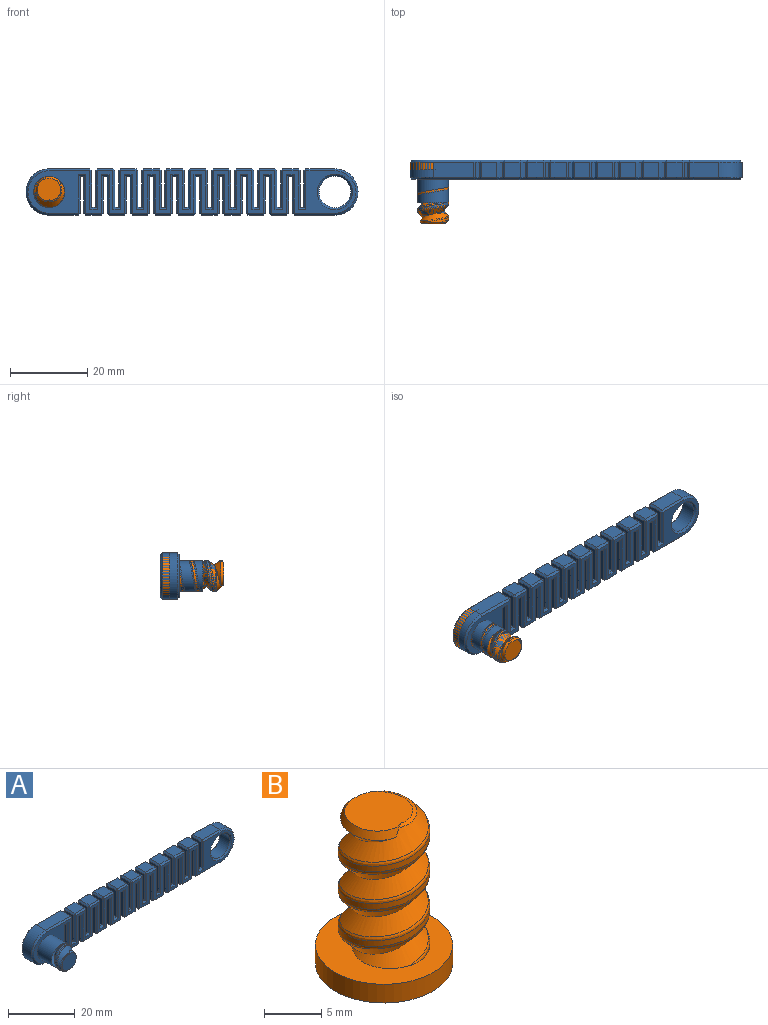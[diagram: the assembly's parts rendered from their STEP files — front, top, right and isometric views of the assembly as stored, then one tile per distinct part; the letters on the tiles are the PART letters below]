
ASSEMBLY  parts=2 mates=1
PART A: 390 faces, bbox 86.7x17.4x12.7 mm
  f0: cylinder r=4mm len=8mm, axis (0,1,0), area 152mm2, adj f1,f5,f91,f383
  f1: cylinder r=4mm len=8mm, axis (0,1,0), area 10.5mm2, adj f0,f4,f5,f386
  f2: bspline ~9.24x8mm, area 25.8mm2, adj f3,f4,f383,f387
  f3: bspline ~9.24x8mm, area 32.1mm2, adj f2,f5,f383,f387,f389
  f4: bspline ~8.01x7.79mm, area 6.7mm2, adj f1,f2,f383,f385
  f5: bspline ~8.01x7.84mm, area 7.4mm2, adj f0,f1,f3,f383,f388
  f6: plane 9.5x4mm, normal (1,0,0), area 38mm2, adj f89,f141,f142,f152
  f7: plane 4x4mm, normal (0,0,1), area 16mm2, adj f131,f132,f142,f143
  f8: plane 9.5x4mm, normal (-1,0,0), area 38mm2, adj f9,f123,f132,f133
  f9: plane 4x1mm, normal (0,0,1), area 4mm2, adj f8,f10,f119,f128
  f10: plane 9.5x4mm, normal (1,0,0), area 38mm2, adj f9,f113,f114,f124
  f11: plane 10.5x4mm, normal (0,0,1), area 42mm2, adj f12,f104,f114,f115
  f12: cylinder r=6mm len=12mm, axis (0,1,0), area 75.4mm2, adj f11,f13,f100,f110
  f13: plane 7.5x4mm, normal (0,0,-1), area 30mm2, adj f12,f96,f97,f105
  f14: plane 9.5x4mm, normal (1,0,0), area 38mm2, adj f15,f93,f97,f98
  f15: plane 4x1mm, normal (0,0,-1), area 4mm2, adj f14,f16,f95,f102
  f16: plane 9.5x4mm, normal (-1,0,0), area 38mm2, adj f15,f99,f106,f107
  f17: plane 4x4mm, normal (0,0,-1), area 16mm2, adj f107,f108,f116,f117
  f18: plane 9.5x4mm, normal (1,0,0), area 38mm2, adj f19,f117,f118,f125
  f19: plane 4x1mm, normal (0,0,-1), area 4mm2, adj f18,f20,f122,f129
  f20: plane 9.5x4mm, normal (-1,0,0), area 38mm2, adj f19,f126,f134,f135
  f21: plane 4x4mm, normal (0,0,-1), area 16mm2, adj f135,f136,f144,f145
  f22: plane 9.5x4mm, normal (1,0,0), area 38mm2, adj f23,f145,f146,f153
  f23: plane 4x1mm, normal (0,0,-1), area 4mm2, adj f22,f24,f150,f157
  f24: plane 9.5x4mm, normal (-1,0,0), area 38mm2, adj f23,f154,f162,f163
  f25: plane 4x4mm, normal (0,0,-1), area 16mm2, adj f163,f164,f172,f173
  f26: plane 9.5x4mm, normal (1,0,0), area 38mm2, adj f27,f173,f174,f181
  f27: plane 4x1mm, normal (0,0,-1), area 4mm2, adj f26,f28,f178,f185
  f28: plane 9.5x4mm, normal (-1,0,0), area 38mm2, adj f27,f182,f190,f191
  f29: plane 4x4mm, normal (0,0,-1), area 16mm2, adj f191,f192,f200,f201
  f30: plane 9.5x4mm, normal (1,0,0), area 38mm2, adj f31,f201,f202,f209
  f31: plane 4x1mm, normal (0,0,-1), area 4mm2, adj f30,f32,f206,f213
  f32: plane 9.5x4mm, normal (-1,0,0), area 38mm2, adj f31,f210,f218,f219
  f33: plane 4x4mm, normal (0,0,-1), area 16mm2, adj f219,f220,f228,f229
  f34: plane 9.5x4mm, normal (1,0,0), area 38mm2, adj f35,f229,f230,f237
  f35: plane 4x1mm, normal (0,0,-1), area 4mm2, adj f34,f36,f234,f241
  f36: plane 9.5x4mm, normal (-1,0,0), area 38mm2, adj f35,f238,f246,f247
  f37: plane 4x4mm, normal (0,0,-1), area 16mm2, adj f247,f248,f256,f257
  f38: plane 9.5x4mm, normal (1,0,0), area 38mm2, adj f39,f257,f258,f265
  f39: plane 4x1mm, normal (0,0,-1), area 4mm2, adj f38,f40,f262,f269
  f40: plane 9.5x4mm, normal (-1,0,0), area 38mm2, adj f39,f266,f274,f275
  f41: plane 4x4mm, normal (0,0,-1), area 16mm2, adj f275,f276,f284,f285
  f42: plane 9.5x4mm, normal (1,0,0), area 38mm2, adj f43,f285,f286,f293
  f43: plane 4x1mm, normal (0,0,-1), area 4mm2, adj f42,f44,f290,f297
  f44: plane 9.5x4mm, normal (-1,0,0), area 38mm2, adj f43,f294,f302,f303
  f45: plane 4x4mm, normal (0,0,-1), area 16mm2, adj f303,f304,f312,f313
  f46: plane 9.5x4mm, normal (1,0,0), area 38mm2, adj f47,f313,f314,f321
  f47: plane 4x1mm, normal (0,0,-1), area 4mm2, adj f46,f48,f318,f325
  f48: plane 9.5x4mm, normal (-1,0,0), area 38mm2, adj f47,f322,f330,f331
  f49: plane 4x4mm, normal (0,0,-1), area 16mm2, adj f331,f332,f340,f341
  f50: plane 9.5x4mm, normal (1,0,0), area 38mm2, adj f51,f341,f342,f349
  f51: plane 4x1mm, normal (0,0,-1), area 4mm2, adj f50,f52,f346,f353
  f52: plane 9.5x4mm, normal (-1,0,0), area 38mm2, adj f51,f350,f358,f359
  f53: plane 10.5x4mm, normal (0,0,-1), area 42mm2, adj f54,f359,f360,f369
  f54: cylinder r=6mm len=12mm, axis (0,1,0), area 75.4mm2, adj f53,f55,f365,f373
  f55: plane 7.5x4mm, normal (0,0,1), area 30mm2, adj f54,f370,f376,f377
  f56: plane 9.5x4mm, normal (-1,0,0), area 38mm2, adj f57,f371,f377,f380
  f57: plane 4x1mm, normal (0,0,1), area 4mm2, adj f56,f58,f366,f378
  f58: plane 9.5x4mm, normal (1,0,0), area 38mm2, adj f57,f361,f367,f375
  f59: plane 4x4mm, normal (0,0,1), area 16mm2, adj f355,f356,f367,f368
  f60: plane 9.5x4mm, normal (-1,0,0), area 38mm2, adj f61,f347,f356,f357
  f61: plane 4x1mm, normal (0,0,1), area 4mm2, adj f60,f62,f343,f352
  f62: plane 9.5x4mm, normal (1,0,0), area 38mm2, adj f61,f337,f338,f348
  f63: plane 4x4mm, normal (0,0,1), area 16mm2, adj f327,f328,f338,f339
  f64: plane 9.5x4mm, normal (-1,0,0), area 38mm2, adj f65,f319,f328,f329
  f65: plane 4x1mm, normal (0,0,1), area 4mm2, adj f64,f66,f315,f324
  f66: plane 9.5x4mm, normal (1,0,0), area 38mm2, adj f65,f309,f310,f320
  f67: plane 4x4mm, normal (0,0,1), area 16mm2, adj f299,f300,f310,f311
  f68: plane 9.5x4mm, normal (-1,0,0), area 38mm2, adj f69,f291,f300,f301
  f69: plane 4x1mm, normal (0,0,1), area 4mm2, adj f68,f70,f287,f296
  f70: plane 9.5x4mm, normal (1,0,0), area 38mm2, adj f69,f281,f282,f292
  f71: plane 4x4mm, normal (0,0,1), area 16mm2, adj f271,f272,f282,f283
  f72: plane 9.5x4mm, normal (-1,0,0), area 38mm2, adj f73,f263,f272,f273
  f73: plane 4x1mm, normal (0,0,1), area 4mm2, adj f72,f74,f259,f268
  f74: plane 9.5x4mm, normal (1,0,0), area 38mm2, adj f73,f253,f254,f264
  f75: plane 4x4mm, normal (0,0,1), area 16mm2, adj f243,f244,f254,f255
  f76: plane 9.5x4mm, normal (-1,0,0), area 38mm2, adj f77,f235,f244,f245
  f77: plane 4x1mm, normal (0,0,1), area 4mm2, adj f76,f78,f231,f240
  f78: plane 9.5x4mm, normal (1,0,0), area 38mm2, adj f77,f225,f226,f236
  f79: plane 4x4mm, normal (0,0,1), area 16mm2, adj f215,f216,f226,f227
  f80: plane 9.5x4mm, normal (-1,0,0), area 38mm2, adj f81,f207,f216,f217
  f81: plane 4x1mm, normal (0,0,1), area 4mm2, adj f80,f82,f203,f212
  f82: plane 9.5x4mm, normal (1,0,0), area 38mm2, adj f81,f197,f198,f208
  f83: plane 4x4mm, normal (0,0,1), area 16mm2, adj f187,f188,f198,f199
  f84: plane 9.5x4mm, normal (-1,0,0), area 38mm2, adj f85,f179,f188,f189
  f85: plane 4x1mm, normal (0,0,1), area 4mm2, adj f84,f86,f175,f184
  f86: plane 9.5x4mm, normal (1,0,0), area 38mm2, adj f85,f169,f170,f180
  f87: plane 4x4mm, normal (0,0,1), area 16mm2, adj f159,f160,f170,f171
  f88: plane 9.5x4mm, normal (-1,0,0), area 38mm2, adj f89,f151,f160,f161
  f89: plane 4x1mm, normal (0,0,1), area 4mm2, adj f6,f88,f147,f156
  f90: cylinder r=4.1mm len=8.2mm, axis (0,1,0), area 103mm2, adj f381,f382
  f91: plane 85x11mm, normal (0,-1,0), area 392.3mm2, adj f0,f93,f95,f96,f99,f100,f104,f108
  f92: plane 85x11mm, normal (0,1,0), area 442.6mm2, adj f98,f102,f105,f106,f110,f115,f116,f124
  f93: plane 10x0.5mm, normal (0.71,-0.71,0), area 6.9mm2, adj f14,f91,f94,f95
  f94: plane 0.5x0.5mm, normal (0.58,-0.58,-0.58), area 0.2mm2, adj f93,f96,f97
  f95: plane 2x0.5mm, normal (0,-0.71,-0.71), area 1.1mm2, adj f15,f91,f93,f99
  f96: plane 7.5x0.5mm, normal (0,-0.71,-0.71), area 5.3mm2, adj f13,f91,f94,f100
  f97: plane 4x0.5mm, normal (0.71,0,-0.71), area 2.8mm2, adj f13,f14,f94,f101
  f98: plane 10x0.5mm, normal (0.71,0.71,0), area 6.9mm2, adj f14,f92,f101,f102
  f99: plane 10x0.5mm, normal (-0.71,-0.71,0), area 6.9mm2, adj f16,f91,f95,f103
  f100: cone r=5.5mm half-angle=45deg, axis (0,1,0), area 12.8mm2, adj f12,f91,f96,f104
  f101: plane 0.5x0.5mm, normal (0.58,0.58,-0.58), area 0.2mm2, adj f97,f98,f105
  f102: plane 2x0.5mm, normal (0,0.71,-0.71), area 1.1mm2, adj f15,f92,f98,f106
  f103: plane 0.5x0.5mm, normal (-0.58,-0.58,-0.58), area 0.2mm2, adj f99,f107,f108
  f104: plane 10.5x0.5mm, normal (0,-0.71,0.71), area 7.4mm2, adj f11,f91,f100,f109
  f105: plane 7.5x0.5mm, normal (0,0.71,-0.71), area 5.3mm2, adj f13,f92,f101,f110
  f106: plane 10x0.5mm, normal (-0.71,0.71,0), area 6.9mm2, adj f16,f92,f102,f111
  f107: plane 4x0.5mm, normal (-0.71,0,-0.71), area 2.8mm2, adj f16,f17,f103,f111
  f108: plane 4x0.5mm, normal (0,-0.71,-0.71), area 2.8mm2, adj f17,f91,f103,f112
  f109: plane 0.5x0.5mm, normal (0.58,-0.58,0.58), area 0.2mm2, adj f104,f113,f114
  f110: cone r=6mm half-angle=45deg, axis (0,-1,0), area 12.8mm2, adj f12,f92,f105,f115
  f111: plane 0.5x0.5mm, normal (-0.58,0.58,-0.58), area 0.2mm2, adj f106,f107,f116
  f112: plane 0.5x0.5mm, normal (0.58,-0.58,-0.58), area 0.2mm2, adj f108,f117,f118
  f113: plane 10x0.5mm, normal (0.71,-0.71,0), area 6.9mm2, adj f10,f91,f109,f119
  f114: plane 4x0.5mm, normal (0.71,0,0.71), area 2.8mm2, adj f10,f11,f109,f120
  f115: plane 10.5x0.5mm, normal (0,0.71,0.71), area 7.4mm2, adj f11,f92,f110,f120
  f116: plane 4x0.5mm, normal (0,0.71,-0.71), area 2.8mm2, adj f17,f92,f111,f121
  f117: plane 4x0.5mm, normal (0.71,0,-0.71), area 2.8mm2, adj f17,f18,f112,f121
  f118: plane 10x0.5mm, normal (0.71,-0.71,0), area 6.9mm2, adj f18,f91,f112,f122
  f119: plane 2x0.5mm, normal (0,-0.71,0.71), area 1.1mm2, adj f9,f91,f113,f123
  f120: plane 0.5x0.5mm, normal (0.58,0.58,0.58), area 0.2mm2, adj f114,f115,f124
  f121: plane 0.5x0.5mm, normal (0.58,0.58,-0.58), area 0.2mm2, adj f116,f117,f125
  f122: plane 2x0.5mm, normal (0,-0.71,-0.71), area 1.1mm2, adj f19,f91,f118,f126
  f123: plane 10x0.5mm, normal (-0.71,-0.71,0), area 6.9mm2, adj f8,f91,f119,f127
  f124: plane 10x0.5mm, normal (0.71,0.71,0), area 6.9mm2, adj f10,f92,f120,f128
  f125: plane 10x0.5mm, normal (0.71,0.71,0), area 6.9mm2, adj f18,f92,f121,f129
  f126: plane 10x0.5mm, normal (-0.71,-0.71,0), area 6.9mm2, adj f20,f91,f122,f130
  f127: plane 0.5x0.5mm, normal (-0.58,-0.58,0.58), area 0.2mm2, adj f123,f131,f132
  f128: plane 2x0.5mm, normal (0,0.71,0.71), area 1.1mm2, adj f9,f92,f124,f133
  f129: plane 2x0.5mm, normal (0,0.71,-0.71), area 1.1mm2, adj f19,f92,f125,f134
  f130: plane 0.5x0.5mm, normal (-0.58,-0.58,-0.58), area 0.2mm2, adj f126,f135,f136
  f131: plane 4x0.5mm, normal (0,-0.71,0.71), area 2.8mm2, adj f7,f91,f127,f137
  f132: plane 4x0.5mm, normal (-0.71,0,0.71), area 2.8mm2, adj f7,f8,f127,f138
  f133: plane 10x0.5mm, normal (-0.71,0.71,0), area 6.9mm2, adj f8,f92,f128,f138
  f134: plane 10x0.5mm, normal (-0.71,0.71,0), area 6.9mm2, adj f20,f92,f129,f139
  f135: plane 4x0.5mm, normal (-0.71,0,-0.71), area 2.8mm2, adj f20,f21,f130,f139
  f136: plane 4x0.5mm, normal (0,-0.71,-0.71), area 2.8mm2, adj f21,f91,f130,f140
  f137: plane 0.5x0.5mm, normal (0.58,-0.58,0.58), area 0.2mm2, adj f131,f141,f142
  f138: plane 0.5x0.5mm, normal (-0.58,0.58,0.58), area 0.2mm2, adj f132,f133,f143
  f139: plane 0.5x0.5mm, normal (-0.58,0.58,-0.58), area 0.2mm2, adj f134,f135,f144
  f140: plane 0.5x0.5mm, normal (0.58,-0.58,-0.58), area 0.2mm2, adj f136,f145,f146
  f141: plane 10x0.5mm, normal (0.71,-0.71,0), area 6.9mm2, adj f6,f91,f137,f147
  f142: plane 4x0.5mm, normal (0.71,0,0.71), area 2.8mm2, adj f6,f7,f137,f148
  f143: plane 4x0.5mm, normal (0,0.71,0.71), area 2.8mm2, adj f7,f92,f138,f148
  f144: plane 4x0.5mm, normal (0,0.71,-0.71), area 2.8mm2, adj f21,f92,f139,f149
  f145: plane 4x0.5mm, normal (0.71,0,-0.71), area 2.8mm2, adj f21,f22,f140,f149
  f146: plane 10x0.5mm, normal (0.71,-0.71,0), area 6.9mm2, adj f22,f91,f140,f150
  f147: plane 2x0.5mm, normal (0,-0.71,0.71), area 1.1mm2, adj f89,f91,f141,f151
  f148: plane 0.5x0.5mm, normal (0.58,0.58,0.58), area 0.2mm2, adj f142,f143,f152
  f149: plane 0.5x0.5mm, normal (0.58,0.58,-0.58), area 0.2mm2, adj f144,f145,f153
  f150: plane 2x0.5mm, normal (0,-0.71,-0.71), area 1.1mm2, adj f23,f91,f146,f154
  f151: plane 10x0.5mm, normal (-0.71,-0.71,0), area 6.9mm2, adj f88,f91,f147,f155
  f152: plane 10x0.5mm, normal (0.71,0.71,0), area 6.9mm2, adj f6,f92,f148,f156
  f153: plane 10x0.5mm, normal (0.71,0.71,0), area 6.9mm2, adj f22,f92,f149,f157
  f154: plane 10x0.5mm, normal (-0.71,-0.71,0), area 6.9mm2, adj f24,f91,f150,f158
  f155: plane 0.5x0.5mm, normal (-0.58,-0.58,0.58), area 0.2mm2, adj f151,f159,f160
  f156: plane 2x0.5mm, normal (0,0.71,0.71), area 1.1mm2, adj f89,f92,f152,f161
  f157: plane 2x0.5mm, normal (0,0.71,-0.71), area 1.1mm2, adj f23,f92,f153,f162
  f158: plane 0.5x0.5mm, normal (-0.58,-0.58,-0.58), area 0.2mm2, adj f154,f163,f164
  f159: plane 4x0.5mm, normal (0,-0.71,0.71), area 2.8mm2, adj f87,f91,f155,f165
  f160: plane 4x0.5mm, normal (-0.71,0,0.71), area 2.8mm2, adj f87,f88,f155,f166
  f161: plane 10x0.5mm, normal (-0.71,0.71,0), area 6.9mm2, adj f88,f92,f156,f166
  f162: plane 10x0.5mm, normal (-0.71,0.71,0), area 6.9mm2, adj f24,f92,f157,f167
  f163: plane 4x0.5mm, normal (-0.71,0,-0.71), area 2.8mm2, adj f24,f25,f158,f167
  f164: plane 4x0.5mm, normal (0,-0.71,-0.71), area 2.8mm2, adj f25,f91,f158,f168
  f165: plane 0.5x0.5mm, normal (0.58,-0.58,0.58), area 0.2mm2, adj f159,f169,f170
  f166: plane 0.5x0.5mm, normal (-0.58,0.58,0.58), area 0.2mm2, adj f160,f161,f171
  f167: plane 0.5x0.5mm, normal (-0.58,0.58,-0.58), area 0.2mm2, adj f162,f163,f172
  f168: plane 0.5x0.5mm, normal (0.58,-0.58,-0.58), area 0.2mm2, adj f164,f173,f174
  f169: plane 10x0.5mm, normal (0.71,-0.71,0), area 6.9mm2, adj f86,f91,f165,f175
  f170: plane 4x0.5mm, normal (0.71,0,0.71), area 2.8mm2, adj f86,f87,f165,f176
  f171: plane 4x0.5mm, normal (0,0.71,0.71), area 2.8mm2, adj f87,f92,f166,f176
  f172: plane 4x0.5mm, normal (0,0.71,-0.71), area 2.8mm2, adj f25,f92,f167,f177
  f173: plane 4x0.5mm, normal (0.71,0,-0.71), area 2.8mm2, adj f25,f26,f168,f177
  f174: plane 10x0.5mm, normal (0.71,-0.71,0), area 6.9mm2, adj f26,f91,f168,f178
  f175: plane 2x0.5mm, normal (0,-0.71,0.71), area 1.1mm2, adj f85,f91,f169,f179
  f176: plane 0.5x0.5mm, normal (0.58,0.58,0.58), area 0.2mm2, adj f170,f171,f180
  f177: plane 0.5x0.5mm, normal (0.58,0.58,-0.58), area 0.2mm2, adj f172,f173,f181
  f178: plane 2x0.5mm, normal (0,-0.71,-0.71), area 1.1mm2, adj f27,f91,f174,f182
  f179: plane 10x0.5mm, normal (-0.71,-0.71,0), area 6.9mm2, adj f84,f91,f175,f183
  f180: plane 10x0.5mm, normal (0.71,0.71,0), area 6.9mm2, adj f86,f92,f176,f184
  f181: plane 10x0.5mm, normal (0.71,0.71,0), area 6.9mm2, adj f26,f92,f177,f185
  f182: plane 10x0.5mm, normal (-0.71,-0.71,0), area 6.9mm2, adj f28,f91,f178,f186
  f183: plane 0.5x0.5mm, normal (-0.58,-0.58,0.58), area 0.2mm2, adj f179,f187,f188
  f184: plane 2x0.5mm, normal (0,0.71,0.71), area 1.1mm2, adj f85,f92,f180,f189
  f185: plane 2x0.5mm, normal (0,0.71,-0.71), area 1.1mm2, adj f27,f92,f181,f190
  f186: plane 0.5x0.5mm, normal (-0.58,-0.58,-0.58), area 0.2mm2, adj f182,f191,f192
  f187: plane 4x0.5mm, normal (0,-0.71,0.71), area 2.8mm2, adj f83,f91,f183,f193
  f188: plane 4x0.5mm, normal (-0.71,0,0.71), area 2.8mm2, adj f83,f84,f183,f194
  f189: plane 10x0.5mm, normal (-0.71,0.71,0), area 6.9mm2, adj f84,f92,f184,f194
  f190: plane 10x0.5mm, normal (-0.71,0.71,0), area 6.9mm2, adj f28,f92,f185,f195
  f191: plane 4x0.5mm, normal (-0.71,0,-0.71), area 2.8mm2, adj f28,f29,f186,f195
  f192: plane 4x0.5mm, normal (0,-0.71,-0.71), area 2.8mm2, adj f29,f91,f186,f196
  f193: plane 0.5x0.5mm, normal (0.58,-0.58,0.58), area 0.2mm2, adj f187,f197,f198
  f194: plane 0.5x0.5mm, normal (-0.58,0.58,0.58), area 0.2mm2, adj f188,f189,f199
  f195: plane 0.5x0.5mm, normal (-0.58,0.58,-0.58), area 0.2mm2, adj f190,f191,f200
  f196: plane 0.5x0.5mm, normal (0.58,-0.58,-0.58), area 0.2mm2, adj f192,f201,f202
  f197: plane 10x0.5mm, normal (0.71,-0.71,0), area 6.9mm2, adj f82,f91,f193,f203
  f198: plane 4x0.5mm, normal (0.71,0,0.71), area 2.8mm2, adj f82,f83,f193,f204
  f199: plane 4x0.5mm, normal (0,0.71,0.71), area 2.8mm2, adj f83,f92,f194,f204
  f200: plane 4x0.5mm, normal (0,0.71,-0.71), area 2.8mm2, adj f29,f92,f195,f205
  f201: plane 4x0.5mm, normal (0.71,0,-0.71), area 2.8mm2, adj f29,f30,f196,f205
  f202: plane 10x0.5mm, normal (0.71,-0.71,0), area 6.9mm2, adj f30,f91,f196,f206
  f203: plane 2x0.5mm, normal (0,-0.71,0.71), area 1.1mm2, adj f81,f91,f197,f207
  f204: plane 0.5x0.5mm, normal (0.58,0.58,0.58), area 0.2mm2, adj f198,f199,f208
  f205: plane 0.5x0.5mm, normal (0.58,0.58,-0.58), area 0.2mm2, adj f200,f201,f209
  f206: plane 2x0.5mm, normal (0,-0.71,-0.71), area 1.1mm2, adj f31,f91,f202,f210
  f207: plane 10x0.5mm, normal (-0.71,-0.71,0), area 6.9mm2, adj f80,f91,f203,f211
  f208: plane 10x0.5mm, normal (0.71,0.71,0), area 6.9mm2, adj f82,f92,f204,f212
  f209: plane 10x0.5mm, normal (0.71,0.71,0), area 6.9mm2, adj f30,f92,f205,f213
  f210: plane 10x0.5mm, normal (-0.71,-0.71,0), area 6.9mm2, adj f32,f91,f206,f214
  f211: plane 0.5x0.5mm, normal (-0.58,-0.58,0.58), area 0.2mm2, adj f207,f215,f216
  f212: plane 2x0.5mm, normal (0,0.71,0.71), area 1.1mm2, adj f81,f92,f208,f217
  f213: plane 2x0.5mm, normal (0,0.71,-0.71), area 1.1mm2, adj f31,f92,f209,f218
  f214: plane 0.5x0.5mm, normal (-0.58,-0.58,-0.58), area 0.2mm2, adj f210,f219,f220
  f215: plane 4x0.5mm, normal (0,-0.71,0.71), area 2.8mm2, adj f79,f91,f211,f221
  f216: plane 4x0.5mm, normal (-0.71,0,0.71), area 2.8mm2, adj f79,f80,f211,f222
  f217: plane 10x0.5mm, normal (-0.71,0.71,0), area 6.9mm2, adj f80,f92,f212,f222
  f218: plane 10x0.5mm, normal (-0.71,0.71,0), area 6.9mm2, adj f32,f92,f213,f223
  f219: plane 4x0.5mm, normal (-0.71,0,-0.71), area 2.8mm2, adj f32,f33,f214,f223
  f220: plane 4x0.5mm, normal (0,-0.71,-0.71), area 2.8mm2, adj f33,f91,f214,f224
  f221: plane 0.5x0.5mm, normal (0.58,-0.58,0.58), area 0.2mm2, adj f215,f225,f226
  f222: plane 0.5x0.5mm, normal (-0.58,0.58,0.58), area 0.2mm2, adj f216,f217,f227
  f223: plane 0.5x0.5mm, normal (-0.58,0.58,-0.58), area 0.2mm2, adj f218,f219,f228
  f224: plane 0.5x0.5mm, normal (0.58,-0.58,-0.58), area 0.2mm2, adj f220,f229,f230
  f225: plane 10x0.5mm, normal (0.71,-0.71,0), area 6.9mm2, adj f78,f91,f221,f231
  f226: plane 4x0.5mm, normal (0.71,0,0.71), area 2.8mm2, adj f78,f79,f221,f232
  f227: plane 4x0.5mm, normal (0,0.71,0.71), area 2.8mm2, adj f79,f92,f222,f232
  f228: plane 4x0.5mm, normal (0,0.71,-0.71), area 2.8mm2, adj f33,f92,f223,f233
  f229: plane 4x0.5mm, normal (0.71,0,-0.71), area 2.8mm2, adj f33,f34,f224,f233
  f230: plane 10x0.5mm, normal (0.71,-0.71,0), area 6.9mm2, adj f34,f91,f224,f234
  f231: plane 2x0.5mm, normal (0,-0.71,0.71), area 1.1mm2, adj f77,f91,f225,f235
  f232: plane 0.5x0.5mm, normal (0.58,0.58,0.58), area 0.2mm2, adj f226,f227,f236
  f233: plane 0.5x0.5mm, normal (0.58,0.58,-0.58), area 0.2mm2, adj f228,f229,f237
  f234: plane 2x0.5mm, normal (0,-0.71,-0.71), area 1.1mm2, adj f35,f91,f230,f238
  f235: plane 10x0.5mm, normal (-0.71,-0.71,0), area 6.9mm2, adj f76,f91,f231,f239
  f236: plane 10x0.5mm, normal (0.71,0.71,0), area 6.9mm2, adj f78,f92,f232,f240
  f237: plane 10x0.5mm, normal (0.71,0.71,0), area 6.9mm2, adj f34,f92,f233,f241
  f238: plane 10x0.5mm, normal (-0.71,-0.71,0), area 6.9mm2, adj f36,f91,f234,f242
  f239: plane 0.5x0.5mm, normal (-0.58,-0.58,0.58), area 0.2mm2, adj f235,f243,f244
  f240: plane 2x0.5mm, normal (0,0.71,0.71), area 1.1mm2, adj f77,f92,f236,f245
  f241: plane 2x0.5mm, normal (0,0.71,-0.71), area 1.1mm2, adj f35,f92,f237,f246
  f242: plane 0.5x0.5mm, normal (-0.58,-0.58,-0.58), area 0.2mm2, adj f238,f247,f248
  f243: plane 4x0.5mm, normal (0,-0.71,0.71), area 2.8mm2, adj f75,f91,f239,f249
  f244: plane 4x0.5mm, normal (-0.71,0,0.71), area 2.8mm2, adj f75,f76,f239,f250
  f245: plane 10x0.5mm, normal (-0.71,0.71,0), area 6.9mm2, adj f76,f92,f240,f250
  f246: plane 10x0.5mm, normal (-0.71,0.71,0), area 6.9mm2, adj f36,f92,f241,f251
  f247: plane 4x0.5mm, normal (-0.71,0,-0.71), area 2.8mm2, adj f36,f37,f242,f251
  f248: plane 4x0.5mm, normal (0,-0.71,-0.71), area 2.8mm2, adj f37,f91,f242,f252
  f249: plane 0.5x0.5mm, normal (0.58,-0.58,0.58), area 0.2mm2, adj f243,f253,f254
  f250: plane 0.5x0.5mm, normal (-0.58,0.58,0.58), area 0.2mm2, adj f244,f245,f255
  f251: plane 0.5x0.5mm, normal (-0.58,0.58,-0.58), area 0.2mm2, adj f246,f247,f256
  f252: plane 0.5x0.5mm, normal (0.58,-0.58,-0.58), area 0.2mm2, adj f248,f257,f258
  f253: plane 10x0.5mm, normal (0.71,-0.71,0), area 6.9mm2, adj f74,f91,f249,f259
  f254: plane 4x0.5mm, normal (0.71,0,0.71), area 2.8mm2, adj f74,f75,f249,f260
  f255: plane 4x0.5mm, normal (0,0.71,0.71), area 2.8mm2, adj f75,f92,f250,f260
  f256: plane 4x0.5mm, normal (0,0.71,-0.71), area 2.8mm2, adj f37,f92,f251,f261
  f257: plane 4x0.5mm, normal (0.71,0,-0.71), area 2.8mm2, adj f37,f38,f252,f261
  f258: plane 10x0.5mm, normal (0.71,-0.71,0), area 6.9mm2, adj f38,f91,f252,f262
  f259: plane 2x0.5mm, normal (0,-0.71,0.71), area 1.1mm2, adj f73,f91,f253,f263
  f260: plane 0.5x0.5mm, normal (0.58,0.58,0.58), area 0.2mm2, adj f254,f255,f264
  f261: plane 0.5x0.5mm, normal (0.58,0.58,-0.58), area 0.2mm2, adj f256,f257,f265
  f262: plane 2x0.5mm, normal (0,-0.71,-0.71), area 1.1mm2, adj f39,f91,f258,f266
  f263: plane 10x0.5mm, normal (-0.71,-0.71,0), area 6.9mm2, adj f72,f91,f259,f267
  f264: plane 10x0.5mm, normal (0.71,0.71,0), area 6.9mm2, adj f74,f92,f260,f268
  f265: plane 10x0.5mm, normal (0.71,0.71,0), area 6.9mm2, adj f38,f92,f261,f269
  f266: plane 10x0.5mm, normal (-0.71,-0.71,0), area 6.9mm2, adj f40,f91,f262,f270
  f267: plane 0.5x0.5mm, normal (-0.58,-0.58,0.58), area 0.2mm2, adj f263,f271,f272
  f268: plane 2x0.5mm, normal (0,0.71,0.71), area 1.1mm2, adj f73,f92,f264,f273
  f269: plane 2x0.5mm, normal (0,0.71,-0.71), area 1.1mm2, adj f39,f92,f265,f274
  f270: plane 0.5x0.5mm, normal (-0.58,-0.58,-0.58), area 0.2mm2, adj f266,f275,f276
  f271: plane 4x0.5mm, normal (0,-0.71,0.71), area 2.8mm2, adj f71,f91,f267,f277
  f272: plane 4x0.5mm, normal (-0.71,0,0.71), area 2.8mm2, adj f71,f72,f267,f278
  f273: plane 10x0.5mm, normal (-0.71,0.71,0), area 6.9mm2, adj f72,f92,f268,f278
  f274: plane 10x0.5mm, normal (-0.71,0.71,0), area 6.9mm2, adj f40,f92,f269,f279
  f275: plane 4x0.5mm, normal (-0.71,0,-0.71), area 2.8mm2, adj f40,f41,f270,f279
  f276: plane 4x0.5mm, normal (0,-0.71,-0.71), area 2.8mm2, adj f41,f91,f270,f280
  f277: plane 0.5x0.5mm, normal (0.58,-0.58,0.58), area 0.2mm2, adj f271,f281,f282
  f278: plane 0.5x0.5mm, normal (-0.58,0.58,0.58), area 0.2mm2, adj f272,f273,f283
  f279: plane 0.5x0.5mm, normal (-0.58,0.58,-0.58), area 0.2mm2, adj f274,f275,f284
  f280: plane 0.5x0.5mm, normal (0.58,-0.58,-0.58), area 0.2mm2, adj f276,f285,f286
  f281: plane 10x0.5mm, normal (0.71,-0.71,0), area 6.9mm2, adj f70,f91,f277,f287
  f282: plane 4x0.5mm, normal (0.71,0,0.71), area 2.8mm2, adj f70,f71,f277,f288
  f283: plane 4x0.5mm, normal (0,0.71,0.71), area 2.8mm2, adj f71,f92,f278,f288
  f284: plane 4x0.5mm, normal (0,0.71,-0.71), area 2.8mm2, adj f41,f92,f279,f289
  f285: plane 4x0.5mm, normal (0.71,0,-0.71), area 2.8mm2, adj f41,f42,f280,f289
  f286: plane 10x0.5mm, normal (0.71,-0.71,0), area 6.9mm2, adj f42,f91,f280,f290
  f287: plane 2x0.5mm, normal (0,-0.71,0.71), area 1.1mm2, adj f69,f91,f281,f291
  f288: plane 0.5x0.5mm, normal (0.58,0.58,0.58), area 0.2mm2, adj f282,f283,f292
  f289: plane 0.5x0.5mm, normal (0.58,0.58,-0.58), area 0.2mm2, adj f284,f285,f293
  f290: plane 2x0.5mm, normal (0,-0.71,-0.71), area 1.1mm2, adj f43,f91,f286,f294
  f291: plane 10x0.5mm, normal (-0.71,-0.71,0), area 6.9mm2, adj f68,f91,f287,f295
  f292: plane 10x0.5mm, normal (0.71,0.71,0), area 6.9mm2, adj f70,f92,f288,f296
  f293: plane 10x0.5mm, normal (0.71,0.71,0), area 6.9mm2, adj f42,f92,f289,f297
  f294: plane 10x0.5mm, normal (-0.71,-0.71,0), area 6.9mm2, adj f44,f91,f290,f298
  f295: plane 0.5x0.5mm, normal (-0.58,-0.58,0.58), area 0.2mm2, adj f291,f299,f300
  f296: plane 2x0.5mm, normal (0,0.71,0.71), area 1.1mm2, adj f69,f92,f292,f301
  f297: plane 2x0.5mm, normal (0,0.71,-0.71), area 1.1mm2, adj f43,f92,f293,f302
  f298: plane 0.5x0.5mm, normal (-0.58,-0.58,-0.58), area 0.2mm2, adj f294,f303,f304
  f299: plane 4x0.5mm, normal (0,-0.71,0.71), area 2.8mm2, adj f67,f91,f295,f305
  f300: plane 4x0.5mm, normal (-0.71,0,0.71), area 2.8mm2, adj f67,f68,f295,f306
  f301: plane 10x0.5mm, normal (-0.71,0.71,0), area 6.9mm2, adj f68,f92,f296,f306
  f302: plane 10x0.5mm, normal (-0.71,0.71,0), area 6.9mm2, adj f44,f92,f297,f307
  f303: plane 4x0.5mm, normal (-0.71,0,-0.71), area 2.8mm2, adj f44,f45,f298,f307
  f304: plane 4x0.5mm, normal (0,-0.71,-0.71), area 2.8mm2, adj f45,f91,f298,f308
  f305: plane 0.5x0.5mm, normal (0.58,-0.58,0.58), area 0.2mm2, adj f299,f309,f310
  f306: plane 0.5x0.5mm, normal (-0.58,0.58,0.58), area 0.2mm2, adj f300,f301,f311
  f307: plane 0.5x0.5mm, normal (-0.58,0.58,-0.58), area 0.2mm2, adj f302,f303,f312
  f308: plane 0.5x0.5mm, normal (0.58,-0.58,-0.58), area 0.2mm2, adj f304,f313,f314
  f309: plane 10x0.5mm, normal (0.71,-0.71,0), area 6.9mm2, adj f66,f91,f305,f315
  f310: plane 4x0.5mm, normal (0.71,0,0.71), area 2.8mm2, adj f66,f67,f305,f316
  f311: plane 4x0.5mm, normal (0,0.71,0.71), area 2.8mm2, adj f67,f92,f306,f316
  f312: plane 4x0.5mm, normal (0,0.71,-0.71), area 2.8mm2, adj f45,f92,f307,f317
  f313: plane 4x0.5mm, normal (0.71,0,-0.71), area 2.8mm2, adj f45,f46,f308,f317
  f314: plane 10x0.5mm, normal (0.71,-0.71,0), area 6.9mm2, adj f46,f91,f308,f318
  f315: plane 2x0.5mm, normal (0,-0.71,0.71), area 1.1mm2, adj f65,f91,f309,f319
  f316: plane 0.5x0.5mm, normal (0.58,0.58,0.58), area 0.2mm2, adj f310,f311,f320
  f317: plane 0.5x0.5mm, normal (0.58,0.58,-0.58), area 0.2mm2, adj f312,f313,f321
  f318: plane 2x0.5mm, normal (0,-0.71,-0.71), area 1.1mm2, adj f47,f91,f314,f322
  f319: plane 10x0.5mm, normal (-0.71,-0.71,0), area 6.9mm2, adj f64,f91,f315,f323
  f320: plane 10x0.5mm, normal (0.71,0.71,0), area 6.9mm2, adj f66,f92,f316,f324
  f321: plane 10x0.5mm, normal (0.71,0.71,0), area 6.9mm2, adj f46,f92,f317,f325
  f322: plane 10x0.5mm, normal (-0.71,-0.71,0), area 6.9mm2, adj f48,f91,f318,f326
  f323: plane 0.5x0.5mm, normal (-0.58,-0.58,0.58), area 0.2mm2, adj f319,f327,f328
  f324: plane 2x0.5mm, normal (0,0.71,0.71), area 1.1mm2, adj f65,f92,f320,f329
  f325: plane 2x0.5mm, normal (0,0.71,-0.71), area 1.1mm2, adj f47,f92,f321,f330
  f326: plane 0.5x0.5mm, normal (-0.58,-0.58,-0.58), area 0.2mm2, adj f322,f331,f332
  f327: plane 4x0.5mm, normal (0,-0.71,0.71), area 2.8mm2, adj f63,f91,f323,f333
  f328: plane 4x0.5mm, normal (-0.71,0,0.71), area 2.8mm2, adj f63,f64,f323,f334
  f329: plane 10x0.5mm, normal (-0.71,0.71,0), area 6.9mm2, adj f64,f92,f324,f334
  f330: plane 10x0.5mm, normal (-0.71,0.71,0), area 6.9mm2, adj f48,f92,f325,f335
  f331: plane 4x0.5mm, normal (-0.71,0,-0.71), area 2.8mm2, adj f48,f49,f326,f335
  f332: plane 4x0.5mm, normal (0,-0.71,-0.71), area 2.8mm2, adj f49,f91,f326,f336
  f333: plane 0.5x0.5mm, normal (0.58,-0.58,0.58), area 0.2mm2, adj f327,f337,f338
  f334: plane 0.5x0.5mm, normal (-0.58,0.58,0.58), area 0.2mm2, adj f328,f329,f339
  f335: plane 0.5x0.5mm, normal (-0.58,0.58,-0.58), area 0.2mm2, adj f330,f331,f340
  f336: plane 0.5x0.5mm, normal (0.58,-0.58,-0.58), area 0.2mm2, adj f332,f341,f342
  f337: plane 10x0.5mm, normal (0.71,-0.71,0), area 6.9mm2, adj f62,f91,f333,f343
  f338: plane 4x0.5mm, normal (0.71,0,0.71), area 2.8mm2, adj f62,f63,f333,f344
  f339: plane 4x0.5mm, normal (0,0.71,0.71), area 2.8mm2, adj f63,f92,f334,f344
  f340: plane 4x0.5mm, normal (0,0.71,-0.71), area 2.8mm2, adj f49,f92,f335,f345
  f341: plane 4x0.5mm, normal (0.71,0,-0.71), area 2.8mm2, adj f49,f50,f336,f345
  f342: plane 10x0.5mm, normal (0.71,-0.71,0), area 6.9mm2, adj f50,f91,f336,f346
  f343: plane 2x0.5mm, normal (0,-0.71,0.71), area 1.1mm2, adj f61,f91,f337,f347
  f344: plane 0.5x0.5mm, normal (0.58,0.58,0.58), area 0.2mm2, adj f338,f339,f348
  f345: plane 0.5x0.5mm, normal (0.58,0.58,-0.58), area 0.2mm2, adj f340,f341,f349
  f346: plane 2x0.5mm, normal (0,-0.71,-0.71), area 1.1mm2, adj f51,f91,f342,f350
  f347: plane 10x0.5mm, normal (-0.71,-0.71,0), area 6.9mm2, adj f60,f91,f343,f351
  f348: plane 10x0.5mm, normal (0.71,0.71,0), area 6.9mm2, adj f62,f92,f344,f352
  f349: plane 10x0.5mm, normal (0.71,0.71,0), area 6.9mm2, adj f50,f92,f345,f353
  f350: plane 10x0.5mm, normal (-0.71,-0.71,0), area 6.9mm2, adj f52,f91,f346,f354
  f351: plane 0.5x0.5mm, normal (-0.58,-0.58,0.58), area 0.2mm2, adj f347,f355,f356
  f352: plane 2x0.5mm, normal (0,0.71,0.71), area 1.1mm2, adj f61,f92,f348,f357
  f353: plane 2x0.5mm, normal (0,0.71,-0.71), area 1.1mm2, adj f51,f92,f349,f358
  f354: plane 0.5x0.5mm, normal (-0.58,-0.58,-0.58), area 0.2mm2, adj f350,f359,f360
  f355: plane 4x0.5mm, normal (0,-0.71,0.71), area 2.8mm2, adj f59,f91,f351,f362
  f356: plane 4x0.5mm, normal (-0.71,0,0.71), area 2.8mm2, adj f59,f60,f351,f363
  f357: plane 10x0.5mm, normal (-0.71,0.71,0), area 6.9mm2, adj f60,f92,f352,f363
  f358: plane 10x0.5mm, normal (-0.71,0.71,0), area 6.9mm2, adj f52,f92,f353,f364
  f359: plane 4x0.5mm, normal (-0.71,0,-0.71), area 2.8mm2, adj f52,f53,f354,f364
  f360: plane 10.5x0.5mm, normal (0,-0.71,-0.71), area 7.4mm2, adj f53,f91,f354,f365
  f361: plane 10x0.5mm, normal (0.71,-0.71,0), area 6.9mm2, adj f58,f91,f362,f366
  f362: plane 0.5x0.5mm, normal (0.58,-0.58,0.58), area 0.2mm2, adj f355,f361,f367
  f363: plane 0.5x0.5mm, normal (-0.58,0.58,0.58), area 0.2mm2, adj f356,f357,f368
  f364: plane 0.5x0.5mm, normal (-0.58,0.58,-0.58), area 0.2mm2, adj f358,f359,f369
  f365: cone r=6mm half-angle=45deg, axis (0,1,0), area 12.8mm2, adj f54,f91,f360,f370
  f366: plane 2x0.5mm, normal (0,-0.71,0.71), area 1.1mm2, adj f57,f91,f361,f371
  f367: plane 4x0.5mm, normal (0.71,0,0.71), area 2.8mm2, adj f58,f59,f362,f372
  f368: plane 4x0.5mm, normal (0,0.71,0.71), area 2.8mm2, adj f59,f92,f363,f372
  f369: plane 10.5x0.5mm, normal (0,0.71,-0.71), area 7.4mm2, adj f53,f92,f364,f373
  f370: plane 7.5x0.5mm, normal (0,-0.71,0.71), area 5.3mm2, adj f55,f91,f365,f374
  f371: plane 10x0.5mm, normal (-0.71,-0.71,0), area 6.9mm2, adj f56,f91,f366,f374
  f372: plane 0.5x0.5mm, normal (0.58,0.58,0.58), area 0.2mm2, adj f367,f368,f375
  f373: cone r=5.5mm half-angle=45deg, axis (0,-1,0), area 12.8mm2, adj f54,f92,f369,f376
  f374: plane 0.5x0.5mm, normal (-0.58,-0.58,0.58), area 0.2mm2, adj f370,f371,f377
  f375: plane 10x0.5mm, normal (0.71,0.71,0), area 6.9mm2, adj f58,f92,f372,f378
  f376: plane 7.5x0.5mm, normal (0,0.71,0.71), area 5.3mm2, adj f55,f92,f373,f379
  f377: plane 4x0.5mm, normal (-0.71,0,0.71), area 2.8mm2, adj f55,f56,f374,f379
  f378: plane 2x0.5mm, normal (0,0.71,0.71), area 1.1mm2, adj f57,f92,f375,f380
  f379: plane 0.5x0.5mm, normal (-0.58,0.58,0.58), area 0.2mm2, adj f376,f377,f380
  f380: plane 10x0.5mm, normal (-0.71,0.71,0), area 6.9mm2, adj f56,f92,f378,f379
  f381: cone r=4.6mm half-angle=45deg, axis (0,-1,0), area 19.3mm2, adj f90,f91
  f382: cone r=4.1mm half-angle=45deg, axis (0,1,0), area 19.3mm2, adj f90,f92
  f383: plane 8.65x8.2mm, normal (0,-1,0), area 11.2mm2, adj f0,f2,f3,f4,f5
  f384: plane 6.08x5.85mm, normal (0,-1,0), area 27.6mm2, adj f385,f386,f387,f388,f389
  f385: bspline ~0.75x0.5mm, area 0.2mm2, adj f4,f384,f386,f387
  f386: cone r=3.55mm half-angle=45deg, axis (0,1,0), area 2.3mm2, adj f1,f384,f385,f388
  f387: bspline ~5.69x4.54mm, area 5.9mm2, adj f2,f3,f384,f385,f389
  f388: bspline ~0.5x0.45mm, area 0.1mm2, adj f5,f384,f386,f389
  f389: bspline ~5.93x3.82mm, area 3.1mm2, adj f3,f384,f387,f388
PART B: 12 faces, bbox 12.6x12.6x18.3 mm
  f0: cylinder r=6mm len=12mm, axis (0,0,-1), area 75.4mm2, adj f1,f2
  f1: plane 12.64x12.64mm, normal (0,0,1), area 74mm2, adj f0,f3,f5,f6,f10,f11
  f2: plane 12x12mm, normal (0,0,-1), area 113.1mm2, adj f0
  f3: cylinder r=4mm len=13.54mm, axis (0,0,-1), area 51.5mm2, adj f1,f8,f9,f10,f11
  f4: plane 6.05x5.79mm, normal (0,0,1), area 27.5mm2, adj f7,f8,f9
  f5: bspline ~16.83x9.24mm, area 124.2mm2, adj f1,f6,f8,f10
  f6: bspline ~17.29x9.24mm, area 130.3mm2, adj f1,f5,f7,f8,f9,f11
  f7: bspline ~6.68x3.81mm, area 2.9mm2, adj f4,f6,f8,f9
  f8: bspline ~6.6x3.62mm, area 6.8mm2, adj f3,f4,f5,f6,f7,f9,f10
  f9: cone r=3.54mm half-angle=45deg, axis (0,0,-1), area 2.5mm2, adj f3,f4,f6,f7,f8,f11
  f10: bspline ~14.01x8.01mm, area 30.5mm2, adj f1,f3,f5,f8
  f11: bspline ~14.35x8.01mm, area 31.3mm2, adj f1,f3,f6,f9
PLACE A t=(-7.91,19.6,-6.45)mm
PLACE B rot(axis=(1,0,0),90deg) t=(-7.91,19.1,-6.45)mm
MATE fastened B.f0 <-> A.f12  axis (0,1,0) through (-7.91,19.1,-6.45)mm
